# Revit family: Accessories-Teknion-CADA_Drawer_Accessory_Tray-R2021
name_source: partatom
category: Furniture
units: mm (PartAtom-declared; Revit-internal decimal feet)

## family parameters
Always vertical = Yes
Cut with Voids When Loaded = No
OmniClass Number = 23.40.20.00
OmniClass Title = General Furniture and Specialties
Room Calculation Point = No
Shared = Yes
Work Plane-Based = No

## types (2) — shared parameters
Assembly Code = E2020200
Manufacturer = Teknion
Manufacturer Fax = 416.661.4586
Part Number = CADA
Product Documentation Link = https://www.teknion.com
Product Line = Chronicle
Product Page URL = https://www.teknion.com
Sustainability Data = https://www.teknion.com
URL = www.teknion.com
Unit Weight URL = http://www.teknion.com
Warranty = http://www.teknion.com
zero-valued in all types: Default Elevation

## per-type parameters (varying)
| type | Cork | Description | Model |
| Standard, No Cork Insert | No | Drawer Accessory Tray, Standard, No Cork Insert | CADAS |
| Cork Divider Insert | Yes | Drawer Accessory Tray, Cork Divider Insert | CADAC |

## geometry (parser evidence)
native form markers: Sweep x3
no freeform markers — native parametric forms only
